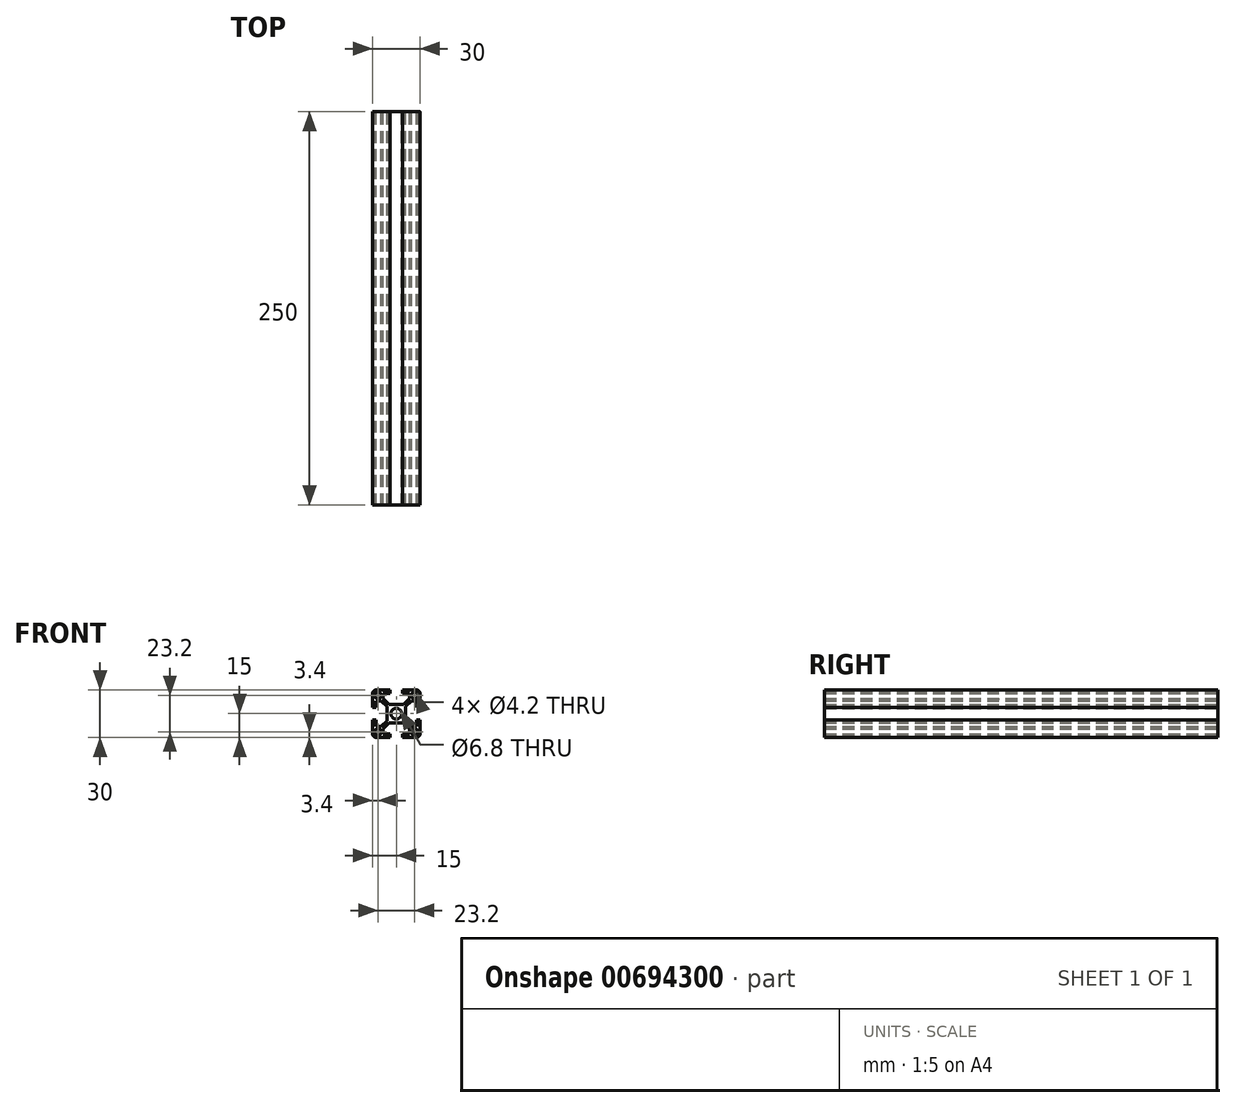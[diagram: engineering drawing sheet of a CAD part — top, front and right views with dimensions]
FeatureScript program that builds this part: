
annotation { "Feature Type Name" : "Feature", "Feature Type Description" : "" }
export const myFeature = defineFeature(function(context is Context, id is Id, definition is map)
    precondition{}
    {
        {
            var Q0;
            Q0=qCreatedBy(makeId("Front.planeOp"),FACE);
            var sketch = newSketch(context, id + "F0", { "sketchPlane" : qUnion([Q0])});
            skLineSegment(sketch, "E0", {"start": v(0, 6) * mm, "end": v(-4.59, 6) * mm});
            skLineSegment(sketch, "E1", {"start": v(-4.59, 6) * mm, "end": v(-8.25, 9.66) * mm});
            skLineSegment(sketch, "E2", {"start": v(-8.25, 9.66) * mm, "end": v(-8.25, 13) * mm});
            skLineSegment(sketch, "E3", {"start": v(-8.25, 13) * mm, "end": v(-4, 13) * mm});
            skLineSegment(sketch, "E4", {"start": v(-4, 13) * mm, "end": v(-4, 15) * mm});
            skLineSegment(sketch, "E5", {"start": v(-4, 15) * mm, "end": v(-13, 15) * mm});
            skLineSegment(sketch, "E6", {"start": v(-15, 13) * mm, "end": v(-15, 4) * mm});
            skLineSegment(sketch, "E7", {"start": v(-15, 4) * mm, "end": v(-13, 4) * mm});
            skLineSegment(sketch, "E8", {"start": v(-13, 4) * mm, "end": v(-13, 8.25) * mm});
            skLineSegment(sketch, "E9", {"start": v(-13, 8.25) * mm, "end": v(-9.66, 8.25) * mm});
            skLineSegment(sketch, "E10", {"start": v(-9.66, 8.25) * mm, "end": v(-6, 4.59) * mm});
            skLineSegment(sketch, "E11", {"start": v(-6, 4.59) * mm, "end": v(-6, 0) * mm});
            skLineSegment(sketch, "E12", {"start": v(-6, 0) * mm, "end": v(0, 0) * mm, "construction": true});
            skLineSegment(sketch, "E13", {"start": v(0, 0) * mm, "end": v(0, 6) * mm, "construction": true});
            skArc(sketch, "E14", {"start": v(0, 3.4) * mm, "mid": v(-2.4, 2.4) * mm, "end": v(-3.4, 0) * mm});
            skCircle(sketch, "E15", {"center": v(-11.6, 11.6) * mm, "radius": 2.1 * mm});
            skLineSegment(sketch, "E16", {"start": v(0, 0) * mm, "end": v(-7.38, 7.38) * mm, "construction": true});
            skLineSegment(sketch, "E17.1.0", {"start": v(-8.25, -13) * mm, "end": v(-8.25, -9.66) * mm});
            skLineSegment(sketch, "E17.1.1", {"start": v(-4, -15) * mm, "end": v(-4, -13) * mm});
            skLineSegment(sketch, "E17.1.2", {"start": v(-4, -13) * mm, "end": v(-8.25, -13) * mm});
            skLineSegment(sketch, "E17.1.3", {"start": v(-15, -4) * mm, "end": v(-15, -13) * mm});
            skLineSegment(sketch, "E17.1.4", {"start": v(-8.25, -9.66) * mm, "end": v(-4.59, -6) * mm});
            skLineSegment(sketch, "E17.1.5", {"start": v(-13, -15) * mm, "end": v(-4, -15) * mm});
            skLineSegment(sketch, "E17.1.6", {"start": v(-4.59, -6) * mm, "end": v(0, -6) * mm});
            skLineSegment(sketch, "E17.1.7", {"start": v(0, -6) * mm, "end": v(0, 0) * mm, "construction": true});
            skLineSegment(sketch, "E17.1.8", {"start": v(0, 0) * mm, "end": v(-6, 0) * mm, "construction": true});
            skLineSegment(sketch, "E17.1.9", {"start": v(-13, -4) * mm, "end": v(-15, -4) * mm});
            skLineSegment(sketch, "E17.1.10", {"start": v(-13, -8.25) * mm, "end": v(-13, -4) * mm});
            skArc(sketch, "E17.1.11", {"start": v(-3.4, 0) * mm, "mid": v(-2.4, -2.4) * mm, "end": v(0, -3.4) * mm});
            skLineSegment(sketch, "E17.1.12", {"start": v(-9.66, -8.25) * mm, "end": v(-13, -8.25) * mm});
            skLineSegment(sketch, "E17.1.13", {"start": v(0, 0) * mm, "end": v(-7.38, -7.38) * mm, "construction": true});
            skLineSegment(sketch, "E17.1.14", {"start": v(-6, -4.59) * mm, "end": v(-9.66, -8.25) * mm});
            skCircle(sketch, "E17.1.15", {"center": v(-11.6, -11.6) * mm, "radius": 2.1 * mm});
            skLineSegment(sketch, "E17.1.16", {"start": v(-6, 0) * mm, "end": v(-6, -4.59) * mm});
            skLineSegment(sketch, "E17.2.0", {"start": v(13, -8.25) * mm, "end": v(9.66, -8.25) * mm});
            skLineSegment(sketch, "E17.2.1", {"start": v(15, -4) * mm, "end": v(13, -4) * mm});
            skLineSegment(sketch, "E17.2.2", {"start": v(13, -4) * mm, "end": v(13, -8.25) * mm});
            skLineSegment(sketch, "E17.2.3", {"start": v(4, -15) * mm, "end": v(13, -15) * mm});
            skLineSegment(sketch, "E17.2.4", {"start": v(9.66, -8.25) * mm, "end": v(6, -4.59) * mm});
            skLineSegment(sketch, "E17.2.5", {"start": v(15, -13) * mm, "end": v(15, -4) * mm});
            skLineSegment(sketch, "E17.2.6", {"start": v(6, -4.59) * mm, "end": v(6, 0) * mm});
            skLineSegment(sketch, "E17.2.7", {"start": v(6, 0) * mm, "end": v(0, 0) * mm, "construction": true});
            skLineSegment(sketch, "E17.2.8", {"start": v(0, 0) * mm, "end": v(0, -6) * mm, "construction": true});
            skLineSegment(sketch, "E17.2.9", {"start": v(4, -13) * mm, "end": v(4, -15) * mm});
            skLineSegment(sketch, "E17.2.10", {"start": v(8.25, -13) * mm, "end": v(4, -13) * mm});
            skArc(sketch, "E17.2.11", {"start": v(0, -3.4) * mm, "mid": v(2.4, -2.4) * mm, "end": v(3.4, 0) * mm});
            skLineSegment(sketch, "E17.2.12", {"start": v(8.25, -9.66) * mm, "end": v(8.25, -13) * mm});
            skLineSegment(sketch, "E17.2.13", {"start": v(0, 0) * mm, "end": v(7.38, -7.38) * mm, "construction": true});
            skLineSegment(sketch, "E17.2.14", {"start": v(4.59, -6) * mm, "end": v(8.25, -9.66) * mm});
            skCircle(sketch, "E17.2.15", {"center": v(11.6, -11.6) * mm, "radius": 2.1 * mm});
            skLineSegment(sketch, "E17.2.16", {"start": v(0, -6) * mm, "end": v(4.59, -6) * mm});
            skLineSegment(sketch, "E17.3.0", {"start": v(8.25, 13) * mm, "end": v(8.25, 9.66) * mm});
            skLineSegment(sketch, "E17.3.1", {"start": v(4, 15) * mm, "end": v(4, 13) * mm});
            skLineSegment(sketch, "E17.3.2", {"start": v(4, 13) * mm, "end": v(8.25, 13) * mm});
            skLineSegment(sketch, "E17.3.3", {"start": v(15, 4) * mm, "end": v(15, 13) * mm});
            skLineSegment(sketch, "E17.3.4", {"start": v(8.25, 9.66) * mm, "end": v(4.59, 6) * mm});
            skLineSegment(sketch, "E17.3.5", {"start": v(13, 15) * mm, "end": v(4, 15) * mm});
            skLineSegment(sketch, "E17.3.6", {"start": v(4.59, 6) * mm, "end": v(0, 6) * mm});
            skLineSegment(sketch, "E17.3.7", {"start": v(0, 6) * mm, "end": v(0, 0) * mm, "construction": true});
            skLineSegment(sketch, "E17.3.8", {"start": v(0, 0) * mm, "end": v(6, 0) * mm, "construction": true});
            skLineSegment(sketch, "E17.3.9", {"start": v(13, 4) * mm, "end": v(15, 4) * mm});
            skLineSegment(sketch, "E17.3.10", {"start": v(13, 8.25) * mm, "end": v(13, 4) * mm});
            skArc(sketch, "E17.3.11", {"start": v(3.4, 0) * mm, "mid": v(2.4, 2.4) * mm, "end": v(0, 3.4) * mm});
            skLineSegment(sketch, "E17.3.12", {"start": v(9.66, 8.25) * mm, "end": v(13, 8.25) * mm});
            skLineSegment(sketch, "E17.3.13", {"start": v(0, 0) * mm, "end": v(7.38, 7.38) * mm, "construction": true});
            skLineSegment(sketch, "E17.3.14", {"start": v(6, 4.59) * mm, "end": v(9.66, 8.25) * mm});
            skCircle(sketch, "E17.3.15", {"center": v(11.6, 11.6) * mm, "radius": 2.1 * mm});
            skLineSegment(sketch, "E17.3.16", {"start": v(6, 0) * mm, "end": v(6, 4.59) * mm});
            skPoint(sketch, "E18.visualSharp", {"position": v(-15, 15) * mm});
            skArc(sketch, "E18.filletArc", {"start": v(-13, 15) * mm, "mid": v(-14.41, 14.41) * mm, "end": v(-15, 13) * mm});
            skPoint(sketch, "E19.visualSharp", {"position": v(15, 15) * mm});
            skArc(sketch, "E19.filletArc", {"start": v(15, 13) * mm, "mid": v(14.41, 14.41) * mm, "end": v(13, 15) * mm});
            skPoint(sketch, "E20.visualSharp", {"position": v(15, -15) * mm});
            skArc(sketch, "E20.filletArc", {"start": v(13, -15) * mm, "mid": v(14.41, -14.41) * mm, "end": v(15, -13) * mm});
            skPoint(sketch, "E21.visualSharp", {"position": v(-15, -15) * mm});
            skArc(sketch, "E21.filletArc", {"start": v(-15, -13) * mm, "mid": v(-14.41, -14.41) * mm, "end": v(-13, -15) * mm});
            skSolve(sketch);
        }
        {
            var Q0;
            Q0=qSketchRegion(id+"F0",true);
            extrude(context, id + "F1", {"entities" : qUnion([Q0]), "depth" : 250 * mm, "offsetDistance" : 25 * mm});
        }
    });
